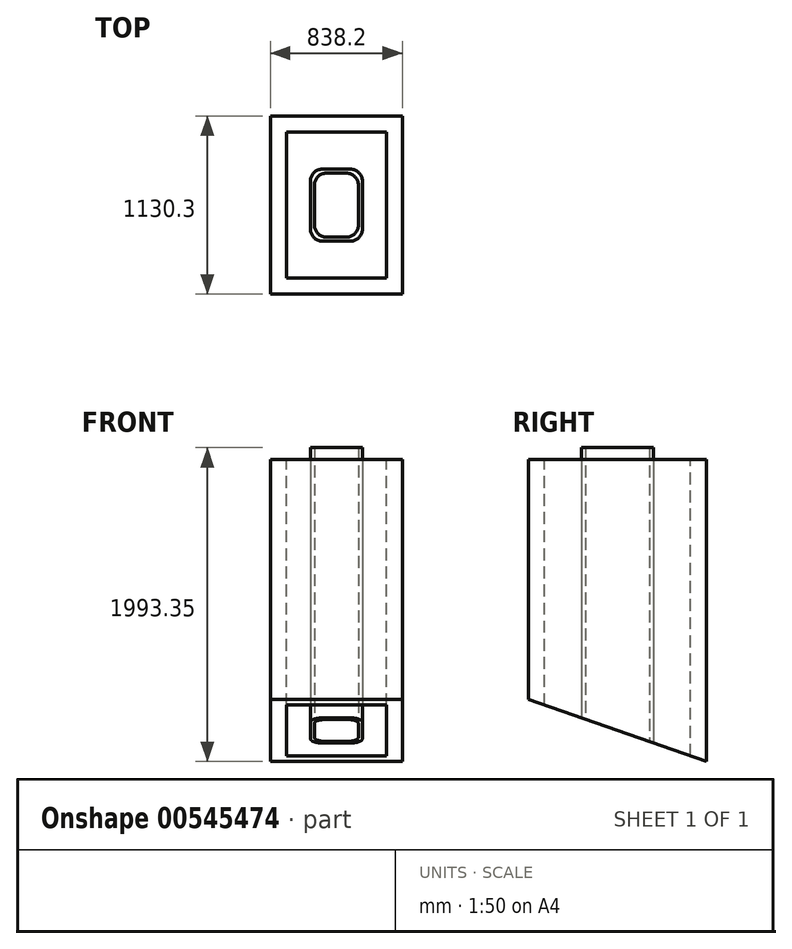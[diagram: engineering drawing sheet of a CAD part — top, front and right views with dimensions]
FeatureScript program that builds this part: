
annotation { "Feature Type Name" : "Feature", "Feature Type Description" : "" }
export const myFeature = defineFeature(function(context is Context, id is Id, definition is map)
    precondition{}
    {
        {
            var Q0;
            Q0=qCreatedBy(makeId("Top.planeOp"),FACE);
            var sketch = newSketch(context, id + "F0", { "sketchPlane" : qUnion([Q0])});
            skLineSegment(sketch, "E0.bottom", {"start": v(-419.1, 565.15) * mm, "end": v(419.1, 565.15) * mm});
            skLineSegment(sketch, "E0.top", {"start": v(-419.1, -565.15) * mm, "end": v(419.1, -565.15) * mm});
            skLineSegment(sketch, "E0.left", {"start": v(-419.1, 565.15) * mm, "end": v(-419.1, -565.15) * mm});
            skLineSegment(sketch, "E0.right", {"start": v(419.1, 565.15) * mm, "end": v(419.1, -565.15) * mm});
            skPoint(sketch, "E0.middle", {"position": v(0, 0) * mm});
            skLineSegment(sketch, "E1.bottom", {"start": v(95.25, 234.95) * mm, "end": v(-95.25, 234.95) * mm});
            skLineSegment(sketch, "E1.top", {"start": v(95.25, -234.95) * mm, "end": v(-95.25, -234.95) * mm});
            skLineSegment(sketch, "E1.left", {"start": v(171.45, 158.75) * mm, "end": v(171.45, -158.75) * mm});
            skLineSegment(sketch, "E1.right", {"start": v(-171.45, 158.75) * mm, "end": v(-171.45, -158.75) * mm});
            skPoint(sketch, "E2.visualSharp", {"position": v(-171.45, -234.95) * mm});
            skArc(sketch, "E2.filletArc", {"start": v(-171.45, -158.75) * mm, "mid": v(-149.13, -212.63) * mm, "end": v(-95.25, -234.95) * mm});
            skPoint(sketch, "E3.visualSharp", {"position": v(171.45, -234.95) * mm});
            skArc(sketch, "E3.filletArc", {"start": v(95.25, -234.95) * mm, "mid": v(149.13, -212.63) * mm, "end": v(171.45, -158.75) * mm});
            skPoint(sketch, "E4.visualSharp", {"position": v(171.45, 234.95) * mm});
            skArc(sketch, "E4.filletArc", {"start": v(171.45, 158.75) * mm, "mid": v(149.13, 212.63) * mm, "end": v(95.25, 234.95) * mm});
            skPoint(sketch, "E5.visualSharp", {"position": v(-171.45, 234.95) * mm});
            skArc(sketch, "E5.filletArc", {"start": v(-95.25, 234.95) * mm, "mid": v(-149.13, 212.63) * mm, "end": v(-171.45, 158.75) * mm});
            skLineSegment(sketch, "E6.bottom", {"start": v(317.5, 463.55) * mm, "end": v(-317.5, 463.55) * mm});
            skLineSegment(sketch, "E6.top", {"start": v(317.5, -463.55) * mm, "end": v(-317.5, -463.55) * mm});
            skLineSegment(sketch, "E6.left", {"start": v(317.5, 463.55) * mm, "end": v(317.5, -463.55) * mm});
            skLineSegment(sketch, "E6.right", {"start": v(-317.5, 463.55) * mm, "end": v(-317.5, -463.55) * mm});
            skLineSegment(sketch, "E7.bottom", {"start": v(425.45, -571.5) * mm, "end": v(-425.45, -571.5) * mm});
            skLineSegment(sketch, "E7.top", {"start": v(425.45, 571.5) * mm, "end": v(-425.45, 571.5) * mm});
            skLineSegment(sketch, "E7.left", {"start": v(425.45, -571.5) * mm, "end": v(425.45, 571.5) * mm});
            skLineSegment(sketch, "E7.right", {"start": v(-425.45, -571.5) * mm, "end": v(-425.45, 571.5) * mm});
            skSolve(sketch);
        }
        {
            var Q0;
            Q0=qCreatedBy(makeId("Right.planeOp"),FACE);
            var sketch = newSketch(context, id + "F1", { "sketchPlane" : qUnion([Q0])});
            skPoint(sketch, "E8.0", {"position": v(-565.15, -1524) * mm});
            skLineSegment(sketch, "E9", {"start": v(-2115.85, -984.63) * mm, "end": v(2208.33, -2488.69) * mm});
            skSolve(sketch);
        }
        {
            var Q0;
            Q0 = qSketchRegion(id + "F1", true);
            var Q1;
            Q1 = qConstructionFilter(qBodyType(qCreatedBy(id + "F1" ,EDGE), BodyType.WIRE), ConstructionObject.NO);
            extrude(context, id + "F2", {"entities" : qUnion([Q0]), "bodyType" : ToolBodyType.SURFACE, "surfaceEntities" : qUnion([Q1]), "depth" : 2540 * mm, "offsetDistance" : 25.4 * mm, "hasSecondDirection" : true, "secondDirectionOppositeDirection" : true, "secondDirectionDepth" : 2540 * mm});
        }
        {
            var Q0;
            Q0=makeQuery(id+"F0.imprint","IMPRINT",FACE,{"disambiguationData":[TD([[makeQuery(id+"F0.imprint","IMPRINT",EDGE,{"derivedFrom":sQuery(id+"F0.wireOp",EDGE,"E0.bottom")}),-1.0]])]});
            extrude(context, id + "F3", {"entities" : qUnion([Q0]), "endBound" : BoundingType.UP_TO_NEXT, "oppositeDirection" : true, "depth" : 1524 * mm, "offsetDistance" : 25.4 * mm});
        }
        {
            var Q0;
            Q0=makeQuery(id+"F0.imprint","IMPRINT",FACE,{"disambiguationData":[TD([[makeQuery(id+"F0.imprint","IMPRINT",EDGE,{"derivedFrom":sQuery(id+"F0.wireOp",EDGE,"E0.bottom")}),-1.0]])]});
            var sketch = newSketch(context, id + "F4", { "sketchPlane" : qUnion([Q0])});
            skLineSegment(sketch, "E10.bottom", {"start": v(88.9, 228.6) * mm, "end": v(-88.9, 228.6) * mm});
            skLineSegment(sketch, "E10.top", {"start": v(88.9, -228.6) * mm, "end": v(-88.9, -228.6) * mm});
            skLineSegment(sketch, "E10.left", {"start": v(165.1, 152.4) * mm, "end": v(165.1, -152.4) * mm});
            skLineSegment(sketch, "E10.right", {"start": v(-165.1, 152.4) * mm, "end": v(-165.1, -152.4) * mm});
            skPoint(sketch, "E10.middle", {"position": v(0, 0) * mm});
            skPoint(sketch, "E11.visualSharp", {"position": v(-165.1, 228.6) * mm});
            skArc(sketch, "E11.filletArc", {"start": v(-88.9, 228.6) * mm, "mid": v(-142.78, 206.28) * mm, "end": v(-165.1, 152.4) * mm});
            skPoint(sketch, "E12.visualSharp", {"position": v(165.1, 228.6) * mm});
            skArc(sketch, "E12.filletArc", {"start": v(165.1, 152.4) * mm, "mid": v(142.78, 206.28) * mm, "end": v(88.9, 228.6) * mm});
            skPoint(sketch, "E13.visualSharp", {"position": v(-165.1, -228.6) * mm});
            skArc(sketch, "E13.filletArc", {"start": v(-165.1, -152.4) * mm, "mid": v(-142.78, -206.28) * mm, "end": v(-88.9, -228.6) * mm});
            skPoint(sketch, "E14.visualSharp", {"position": v(165.1, -228.6) * mm});
            skArc(sketch, "E14.filletArc", {"start": v(88.9, -228.6) * mm, "mid": v(142.78, -206.28) * mm, "end": v(165.1, -152.4) * mm});
            skLineSegment(sketch, "E15.bottom", {"start": v(63.5, 203.2) * mm, "end": v(-63.5, 203.2) * mm});
            skLineSegment(sketch, "E15.top", {"start": v(63.5, -203.2) * mm, "end": v(-63.5, -203.2) * mm});
            skLineSegment(sketch, "E15.left", {"start": v(139.7, 127) * mm, "end": v(139.7, -127) * mm});
            skLineSegment(sketch, "E15.right", {"start": v(-139.7, 127) * mm, "end": v(-139.7, -127) * mm});
            skPoint(sketch, "E16.visualSharp", {"position": v(-139.7, 203.2) * mm});
            skArc(sketch, "E16.filletArc", {"start": v(-63.5, 203.2) * mm, "mid": v(-117.38, 180.88) * mm, "end": v(-139.7, 127) * mm});
            skPoint(sketch, "E17.visualSharp", {"position": v(-139.7, -203.2) * mm});
            skArc(sketch, "E17.filletArc", {"start": v(-139.7, -127) * mm, "mid": v(-117.38, -180.88) * mm, "end": v(-63.5, -203.2) * mm});
            skPoint(sketch, "E18.visualSharp", {"position": v(139.7, -203.2) * mm});
            skArc(sketch, "E18.filletArc", {"start": v(63.5, -203.2) * mm, "mid": v(117.38, -180.88) * mm, "end": v(139.7, -127) * mm});
            skPoint(sketch, "E19.visualSharp", {"position": v(139.7, 203.2) * mm});
            skArc(sketch, "E19.filletArc", {"start": v(139.7, 127) * mm, "mid": v(117.38, 180.88) * mm, "end": v(63.5, 203.2) * mm});
            skSolve(sketch);
        }
        {
            var Q0;
            Q0 = qSketchRegion(id + "F4", true);
            extrude(context, id + "F5", {"entities" : qUnion([Q0]), "depth" : 76.2 * mm, "offsetDistance" : 25.4 * mm, "hasSecondDirection" : true, "secondDirectionBound" : SecondDirectionBoundingType.UP_TO_NEXT, "secondDirectionOppositeDirection" : true, "secondDirectionDepth" : 25.4 * mm});
        }
        {
            var Q0;
            Q0=sQuery(id+"F0.wireOp",EDGE,"E7.left");
            cPoint(context, id + "F6", {"entities" : qUnion([Q0]), "parameter" : 0.5});
        }
        {
            var Q0;
            Q0=qCreatedBy(makeId("Right.planeOp"),FACE);
            var Q1;
            Q1 = qCreatedBy(id + "F6" ,VERTEX);
            cPlane(context, id + "F7", {"entities" : qUnion([Q0, Q1]), "cplaneType" : CPlaneType.PLANE_POINT, "offset" : 25.4 * mm, "width" : 152.4 * mm, "height" : 152.4 * mm});
        }
        {
            var Q0;
            Q0=sQuery(id+"F0.wireOp",EDGE,"E7.right");
            cPoint(context, id + "F8", {"entities" : qUnion([Q0]), "parameter" : 0.5});
        }
        {
            var Q0;
            Q0=qCreatedBy(makeId("Right.planeOp"),FACE);
            var Q1;
            Q1 = qCreatedBy(id + "F8" ,VERTEX);
            cPlane(context, id + "F9", {"entities" : qUnion([Q0, Q1]), "cplaneType" : CPlaneType.PLANE_POINT, "offset" : 25.4 * mm, "width" : 152.4 * mm, "height" : 152.4 * mm});
        }
        {
            var Q0;
            Q0=qCreatedBy(id+"F7.planeOp",FACE);
            var sketch = newSketch(context, id + "F10", { "sketchPlane" : qUnion([Q0])});
            skPoint(sketch, "E20.0", {"position": v(-571.5, 0) * mm});
            skPoint(sketch, "E20.1", {"position": v(571.5, 0) * mm});
            skLineSegment(sketch, "E21.bottom", {"start": v(-571.5, 0) * mm, "end": v(571.5, 0) * mm});
            skLineSegment(sketch, "E21.top", {"start": v(-571.5, -152.4) * mm, "end": v(571.5, -152.4) * mm});
            skLineSegment(sketch, "E21.left", {"start": v(-571.5, 0) * mm, "end": v(-571.5, -152.4) * mm});
            skLineSegment(sketch, "E21.right", {"start": v(571.5, 0) * mm, "end": v(571.5, -152.4) * mm});
            skSolve(sketch);
        }
        {
            var Q0;
            Q0=qCreatedBy(id+"F9.planeOp",FACE);
            var sketch = newSketch(context, id + "F11", { "sketchPlane" : qUnion([Q0])});
            skPoint(sketch, "E22.0", {"position": v(571.5, 0) * mm});
            skPoint(sketch, "E22.1", {"position": v(-571.5, 0) * mm});
            skLineSegment(sketch, "E23.bottom", {"start": v(571.5, 0) * mm, "end": v(-571.5, 0) * mm});
            skLineSegment(sketch, "E23.top", {"start": v(571.5, -152.4) * mm, "end": v(-571.5, -152.4) * mm});
            skLineSegment(sketch, "E23.left", {"start": v(571.5, 0) * mm, "end": v(571.5, -152.4) * mm});
            skLineSegment(sketch, "E23.right", {"start": v(-571.5, 0) * mm, "end": v(-571.5, -152.4) * mm});
            skSolve(sketch);
        }
        {
            var Q0;
            Q0=sQuery(id+"F0.wireOp",EDGE,"E7.bottom");
            cPoint(context, id + "F12", {"entities" : qUnion([Q0]), "parameter" : 0.5});
        }
        {
            var Q0;
            Q0=qCreatedBy(makeId("Front.planeOp"),FACE);
            var Q1;
            Q1 = qCreatedBy(id + "F12" ,VERTEX);
            cPlane(context, id + "F13", {"entities" : qUnion([Q0, Q1]), "cplaneType" : CPlaneType.PLANE_POINT, "offset" : 25.4 * mm, "width" : 152.4 * mm, "height" : 152.4 * mm});
        }
        {
            var Q0;
            Q0=sQuery(id+"F0.wireOp",EDGE,"E7.top");
            cPoint(context, id + "F14", {"entities" : qUnion([Q0]), "parameter" : 0.5});
        }
        {
            var Q0;
            Q0=qCreatedBy(makeId("Front.planeOp"),FACE);
            var Q1;
            Q1 = qCreatedBy(id + "F14" ,VERTEX);
            cPlane(context, id + "F15", {"entities" : qUnion([Q0, Q1]), "cplaneType" : CPlaneType.PLANE_POINT, "offset" : 25.4 * mm, "width" : 152.4 * mm, "height" : 152.4 * mm});
        }
        {
            var Q0;
            Q0=qCreatedBy(id+"F13.planeOp",FACE);
            var sketch = newSketch(context, id + "F16", { "sketchPlane" : qUnion([Q0])});
            skLineSegment(sketch, "E24.0", {"start": v(-425.45, 0) * mm, "end": v(-425.45, -152.4) * mm});
            skLineSegment(sketch, "E24.1", {"start": v(425.45, 0) * mm, "end": v(-425.45, 0) * mm});
            skLineSegment(sketch, "E24.2", {"start": v(425.45, 0) * mm, "end": v(425.45, -152.4) * mm});
            skLineSegment(sketch, "E25", {"start": v(-425.45, -152.4) * mm, "end": v(425.45, -152.4) * mm});
            skSolve(sketch);
        }
        {
            var Q0;
            Q0=qCreatedBy(id+"F15.planeOp",FACE);
            var sketch = newSketch(context, id + "F17", { "sketchPlane" : qUnion([Q0])});
            skLineSegment(sketch, "E26.0", {"start": v(425.45, 0) * mm, "end": v(425.45, -152.4) * mm});
            skLineSegment(sketch, "E26.1", {"start": v(425.45, 0) * mm, "end": v(-425.45, 0) * mm});
            skLineSegment(sketch, "E26.2", {"start": v(-425.45, 0) * mm, "end": v(-425.45, -152.4) * mm});
            skLineSegment(sketch, "E27", {"start": v(425.45, -152.4) * mm, "end": v(-425.45, -152.4) * mm});
            skSolve(sketch);
        }
        {
            var Q0;
            Q0 = qConstructionFilter(qBodyType(qCreatedBy(id + "F16" ,EDGE), BodyType.WIRE), ConstructionObject.NO);
            extrude(context, id + "F18", {"bodyType" : ToolBodyType.SURFACE, "surfaceEntities" : qUnion([Q0]), "depth" : 1.27 * mm, "offsetDistance" : 25.4 * mm});
        }
        {
            var Q0;
            Q0=makeQuery(id+"F10.imprint","IMPRINT",FACE,{"disambiguationData":[TD([[makeQuery(id+"F10.imprint","IMPRINT",EDGE,{"derivedFrom":sQuery(id+"F10.wireOp",EDGE,"E21.bottom")}),-1.0]])]});
            var Q1;
            Q1 = qConstructionFilter(qBodyType(qCreatedBy(id + "F17" ,EDGE), BodyType.WIRE), ConstructionObject.NO);
            extrude(context, id + "F19", {"entities" : qUnion([Q0]), "bodyType" : ToolBodyType.SURFACE, "surfaceEntities" : qUnion([Q1]), "oppositeDirection" : true, "depth" : 1.27 * mm, "offsetDistance" : 25.4 * mm});
        }
    });
